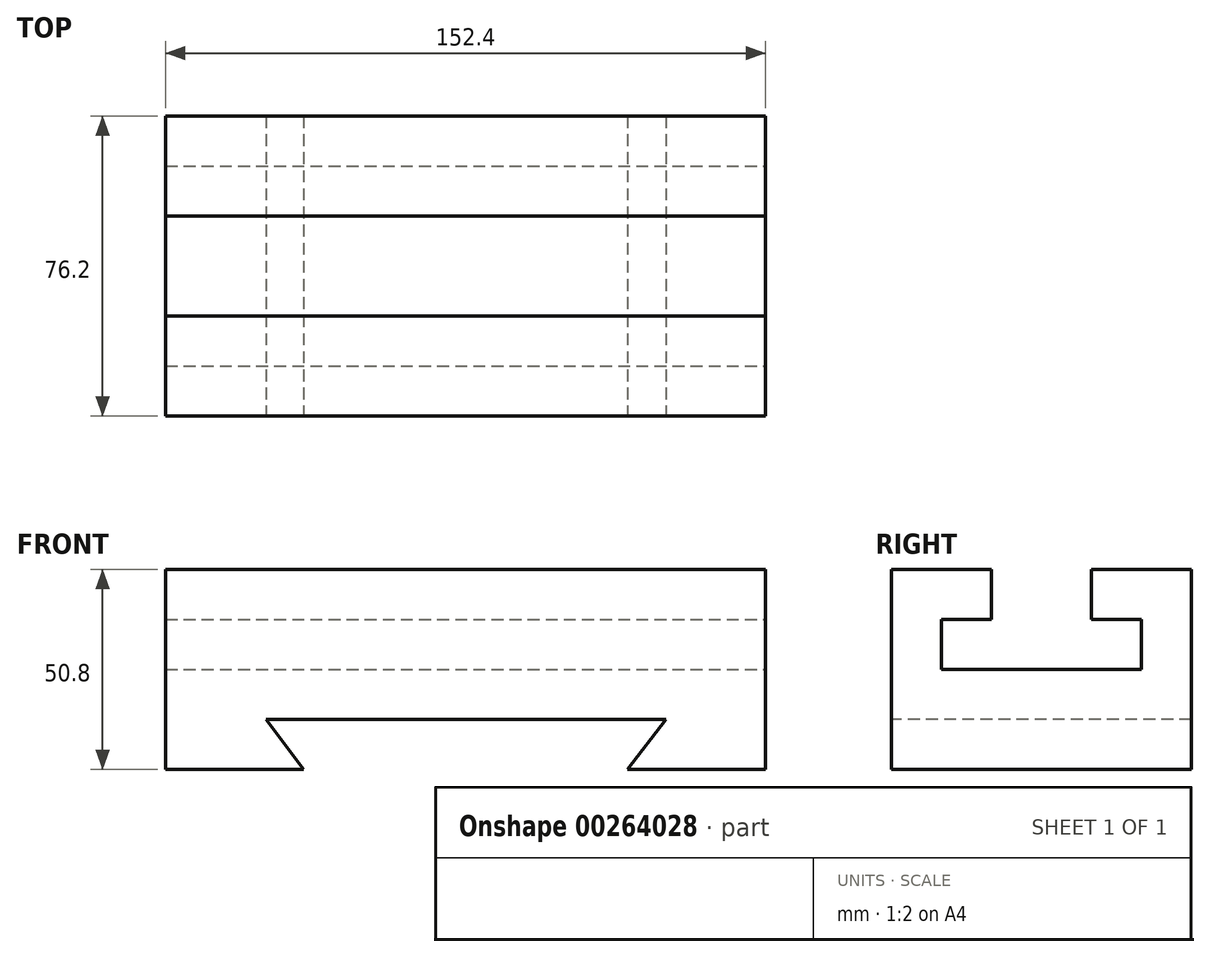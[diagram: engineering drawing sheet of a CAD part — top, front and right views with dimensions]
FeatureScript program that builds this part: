
annotation { "Feature Type Name" : "Feature", "Feature Type Description" : "" }
export const myFeature = defineFeature(function(context is Context, id is Id, definition is map)
    precondition{}
    {
        {
            var Q0;
            Q0=qCreatedBy(makeId("Front.planeOp"),FACE);
            var sketch = newSketch(context, id + "F0", { "sketchPlane" : qUnion([Q0])});
            skLineSegment(sketch, "E0.bottom", {"start": v(-76.27, 0) * mm, "end": v(76.13, 0) * mm});
            skLineSegment(sketch, "E0.top", {"start": v(-76.27, 50.8) * mm, "end": v(76.13, 50.8) * mm});
            skLineSegment(sketch, "E0.left", {"start": v(-76.27, 0) * mm, "end": v(-76.27, 50.8) * mm});
            skLineSegment(sketch, "E0.right", {"start": v(76.13, 0) * mm, "end": v(76.13, 50.8) * mm});
            skSolve(sketch);
        }
        {
            var Q0;
            Q0=makeQuery(id+"F0.imprint","IMPRINT",FACE,{"disambiguationData":[TD([[makeQuery(id+"F0.imprint","IMPRINT",EDGE,{"derivedFrom":sQuery(id+"F0.wireOp",EDGE,"E0.bottom")}),1.0]])]});
            extrude(context, id + "F1", {"entities" : qUnion([Q0]), "depth" : 76.2 * mm});
        }
        {
            var Q0;
            Q0=makeQuery(id+"F1.opExtrude","CAP_FACE",FACE,{"disambiguationData":[OSD([sQuery(id+"F0.wireOp",EDGE,"E0.bottom"),sQuery(id+"F0.wireOp",EDGE,"E0.top"),sQuery(id+"F0.wireOp",EDGE,"E0.left"),sQuery(id+"F0.wireOp",EDGE,"E0.right")])],"isStart":false});
            var sketch = newSketch(context, id + "F2", { "sketchPlane" : qUnion([Q0])});
            skLineSegment(sketch, "E1", {"start": v(0, 0) * mm, "end": v(0, 12.7) * mm});
            skLineSegment(sketch, "E2", {"start": v(0, 12.7) * mm, "end": v(-50.8, 12.7) * mm});
            skLineSegment(sketch, "E3", {"start": v(-50.8, 12.7) * mm, "end": v(50.8, 12.7) * mm});
            skLineSegment(sketch, "E4", {"start": v(50.8, 12.7) * mm, "end": v(41.12, 0) * mm});
            skLineSegment(sketch, "E5", {"start": v(41.12, 0) * mm, "end": v(50.8, 12.7) * mm});
            skLineSegment(sketch, "E6", {"start": v(-50.8, 12.7) * mm, "end": v(-41.2, 0) * mm});
            skLineSegment(sketch, "E7", {"start": v(-41.2, 0) * mm, "end": v(41.12, 0) * mm});
            skSolve(sketch);
        }
        {
            var Q0;
            {var subQ0=sQuery(id+"F2.wireOp",EDGE,"E1");Q0=makeQuery(id+"F2.imprint","IMPRINT",FACE,{"disambiguationData":[TD([[makeQuery(id+"F2.imprint","IMPRINT",EDGE,{"derivedFrom":subQ0}),-1.0]])]});}
            var Q1;
            {var subQ0=sQuery(id+"F2.wireOp",EDGE,"E1");Q1=makeQuery(id+"F2.imprint","IMPRINT",FACE,{"disambiguationData":[TD([[makeQuery(id+"F2.imprint","IMPRINT",EDGE,{"derivedFrom":subQ0}),1.0]])]});}
            extrude(context, id + "F3", {"entities" : qUnion([Q0, Q1]), "operationType" : NewBodyOperationType.REMOVE, "endBound" : BoundingType.UP_TO_NEXT, "oppositeDirection" : true, "depth" : 25.4 * mm});
        }
        {
            var Q0;
            Q0=makeQuery(id+"F1.opExtrude","SWEPT_FACE",FACE,{"disambiguationData":[OSD([sQuery(id+"F0.wireOp",EDGE,"E0.right")])]});
            var sketch = newSketch(context, id + "F4", { "sketchPlane" : qUnion([Q0])});
            skPoint(sketch, "E8.endSnap0", {"position": v(0, 25.4) * mm});
            skLineSegment(sketch, "E9", {"start": v(-12.7, 25.4) * mm, "end": v(-12.7, 38.1) * mm});
            skPoint(sketch, "E10.start.orphan", {"position": v(-17.2, 50.8) * mm});
            skLineSegment(sketch, "E11", {"start": v(-12.7, 38.1) * mm, "end": v(-25.4, 38.1) * mm});
            skLineSegment(sketch, "E12", {"start": v(-25.4, 38.1) * mm, "end": v(-25.4, 50.8) * mm});
            skLineSegment(sketch, "E13", {"start": v(-25.4, 50.8) * mm, "end": v(-50.8, 50.8) * mm});
            skLineSegment(sketch, "E14", {"start": v(-50.8, 50.8) * mm, "end": v(-49.57, 50.8) * mm});
            skLineSegment(sketch, "E15", {"start": v(-50.8, 50.8) * mm, "end": v(-50.8, 38.1) * mm});
            skLineSegment(sketch, "E16", {"start": v(-50.8, 38.1) * mm, "end": v(-63.5, 38.1) * mm});
            skLineSegment(sketch, "E17", {"start": v(-63.5, 38.1) * mm, "end": v(-63.5, 25.4) * mm});
            skLineSegment(sketch, "E18", {"start": v(-63.5, 25.4) * mm, "end": v(-12.7, 25.4) * mm});
            skPoint(sketch, "E8.start.orphan", {"position": v(0, 25.4) * mm});
            skPoint(sketch, "E19.start.orphan", {"position": v(-76.2, 25.4) * mm});
            skSolve(sketch);
        }
        {
            var Q0;
            Q0=makeQuery(id+"F4.imprint","IMPRINT",FACE,{"disambiguationData":[TD([[makeQuery(id+"F4.imprint","IMPRINT",EDGE,{"derivedFrom":sQuery(id+"F4.wireOp",EDGE,"E9")}),1.0]])]});
            extrude(context, id + "F5", {"entities" : qUnion([Q0]), "operationType" : NewBodyOperationType.REMOVE, "endBound" : BoundingType.UP_TO_NEXT, "oppositeDirection" : true, "depth" : 25.4 * mm});
        }
    });
